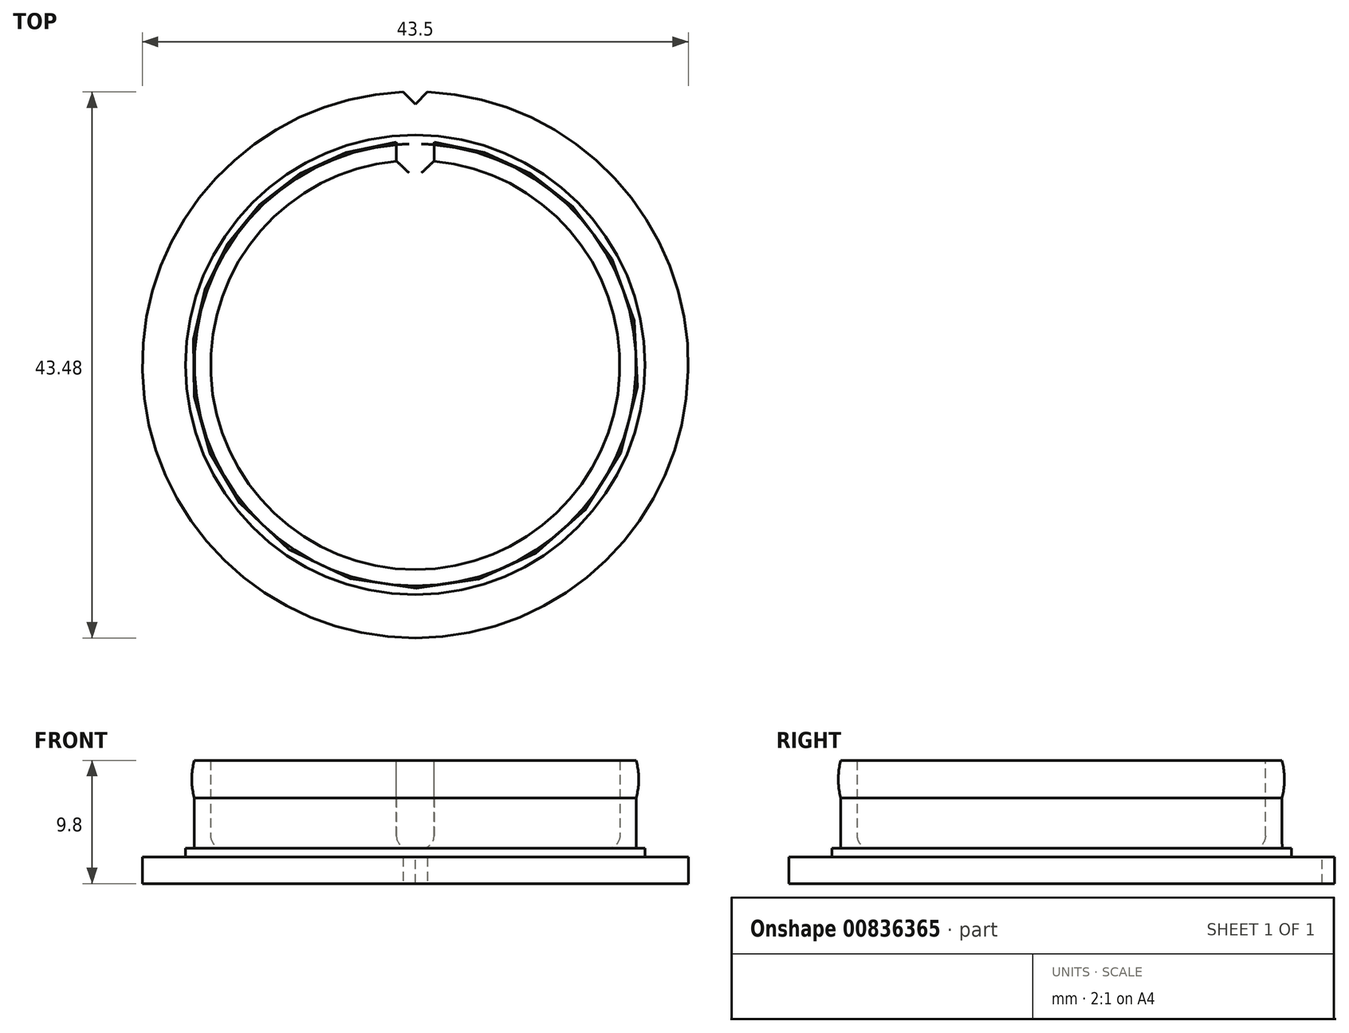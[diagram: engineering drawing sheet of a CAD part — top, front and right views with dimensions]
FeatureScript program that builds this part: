
annotation { "Feature Type Name" : "Feature", "Feature Type Description" : "" }
export const myFeature = defineFeature(function(context is Context, id is Id, definition is map)
    precondition{}
    {
        {
            var Q0;
            Q0=qCreatedBy(makeId("Top.planeOp"),FACE);
            var sketch = newSketch(context, id + "F0", { "sketchPlane" : qUnion([Q0])});
            skCircle(sketch, "E0", {"center": v(0, 0) * mm, "radius": 21.75 * mm});
            skSolve(sketch);
        }
        {
            var Q0;
            Q0 = qSketchRegion(id + "F0", true);
            extrude(context, id + "F1", {"entities" : qUnion([Q0]), "depth" : 2.1 * mm, "offsetDistance" : 25 * mm});
        }
        {
            var Q0;
            Q0=makeQuery(id+"F1.opExtrude","CAP_FACE",FACE,{"disambiguationData":[OSD([sQuery(id+"F0.wireOp",EDGE,"E0")])],"isStart":false});
            var sketch = newSketch(context, id + "F2", { "sketchPlane" : qUnion([Q0])});
            skCircle(sketch, "E1", {"center": v(0, 0) * mm, "radius": 18.3 * mm});
            skSolve(sketch);
        }
        {
            var Q0;
            Q0 = qSketchRegion(id + "F2", true);
            extrude(context, id + "F3", {"entities" : qUnion([Q0]), "operationType" : NewBodyOperationType.ADD, "depth" : .7 * mm, "offsetDistance" : 25 * mm});
        }
        {
            var Q0;
            Q0=makeQuery(id+"F3.opExtrude","CAP_FACE",FACE,{"disambiguationData":[OSD([sQuery(id+"F2.wireOp",EDGE,"E1")])],"isStart":false});
            var sketch = newSketch(context, id + "F4", { "sketchPlane" : qUnion([Q0])});
            skCircle(sketch, "E2", {"center": v(0, 0) * mm, "radius": 17.6 * mm});
            skCircle(sketch, "E3.0", {"center": v(0, 0) * mm, "radius": 16.3 * mm});
            skSolve(sketch);
        }
        {
            var Q0;
            Q0 = qSketchRegion(id + "F4", true);
            extrude(context, id + "F5", {"entities" : qUnion([Q0]), "operationType" : NewBodyOperationType.ADD, "depth" : 7 * mm, "offsetDistance" : 25 * mm});
        }
        {
            var Q0;
            Q0=qCreatedBy(makeId("Front.planeOp"),FACE);
            var sketch = newSketch(context, id + "F6", { "sketchPlane" : qUnion([Q0])});
            skArc(sketch, "E4", {"start": v(-17.6, 9.8) * mm, "mid": v(-17.8, 8.3) * mm, "end": v(-17.6, 6.8) * mm});
            skLineSegment(sketch, "E5", {"start": v(-17.8, 10.53) * mm, "end": v(-17.8, 6.3) * mm, "construction": true});
            skLineSegment(sketch, "E6", {"start": v(-17.6, 9.8) * mm, "end": v(-17.6, 6.8) * mm});
            skSolve(sketch);
        }
        {
            var Q0;
            Q0 = qSketchRegion(id + "F6", true);
            var Q1;
            Q1=makeQuery(id+"F5.opExtrude","SWEPT_FACE",FACE,{"disambiguationData":[OSD([sQuery(id+"F4.wireOp",EDGE,"E2")])]});
            revolve(context, id + "F7", {"operationType" : NewBodyOperationType.ADD, "surfaceOperationType" : NewSurfaceOperationType.NEW, "entities" : qUnion([Q0]), "axis" : qUnion([Q1]), "revolveType" : RevolveType.FULL});
        }
        {
            var Q0;
            Q0=makeQuery(id+"F5.opExtrude","CAP_FACE",FACE,{"disambiguationData":[OSD([sQuery(id+"F4.wireOp",EDGE,"E2"),sQuery(id+"F4.wireOp",EDGE,"E3.0")])],"isStart":false});
            var sketch = newSketch(context, id + "F8", { "sketchPlane" : qUnion([Q0])});
            skLineSegment(sketch, "E7.bottom", {"start": v(-1.5, 19.1) * mm, "end": v(1.5, 19.1) * mm});
            skLineSegment(sketch, "E7.top", {"start": v(-1.5, 16.23) * mm, "end": v(1.5, 16.23) * mm});
            skLineSegment(sketch, "E7.left", {"start": v(-1.5, 19.1) * mm, "end": v(-1.5, 16.23) * mm});
            skLineSegment(sketch, "E7.right", {"start": v(1.5, 19.1) * mm, "end": v(1.5, 16.23) * mm});
            skPoint(sketch, "E8", {"position": v(0, 16.23) * mm});
            skSolve(sketch);
        }
        {
            var Q0;
            Q0 = qSketchRegion(id + "F8", true);
            var Q1;
            {var subQ0=sQuery(id+"F2.wireOp",EDGE,"E1");Q1=makeQuery(id+"F5.boolean.opBoolean","SPLIT",FACE,{"disambiguationData":[TD([makeQuery(id+"F3.opExtrude","SWEPT_FACE",FACE,{"disambiguationData":[OSD([subQ0])]})])],"derivedFrom":makeQuery(id+"F3.opExtrude","CAP_FACE",FACE,{"disambiguationData":[OSD([subQ0])],"isStart":false})});}
            extrude(context, id + "F9", {"entities" : qUnion([Q0]), "operationType" : NewBodyOperationType.REMOVE, "endBound" : BoundingType.UP_TO_SURFACE, "oppositeDirection" : true, "depth" : 25 * mm, "endBoundEntityFace" : qUnion([Q1]), "offsetDistance" : 25 * mm});
        }
        {
            var Q0;
            Q0=makeQuery(id+"F1.opExtrude","CAP_FACE",FACE,{"disambiguationData":[OSD([sQuery(id+"F0.wireOp",EDGE,"E0")])],"isStart":false});
            var sketch = newSketch(context, id + "F10", { "sketchPlane" : qUnion([Q0])});
            skLineSegment(sketch, "E9", {"start": v(0, 20.75) * mm, "end": v(1, 21.75) * mm});
            skLineSegment(sketch, "E10", {"start": v(1, 21.75) * mm, "end": v(-1, 21.75) * mm});
            skLineSegment(sketch, "E11", {"start": v(-1, 21.75) * mm, "end": v(0, 20.75) * mm});
            skSolve(sketch);
        }
        {
            var Q0;
            Q0 = qSketchRegion(id + "F10", true);
            extrude(context, id + "F11", {"entities" : qUnion([Q0]), "operationType" : NewBodyOperationType.REMOVE, "endBound" : BoundingType.THROUGH_ALL, "oppositeDirection" : true, "depth" : 25 * mm, "offsetDistance" : 25 * mm});
        }
        {
            var Q0;
            {var subQ1=sQuery(id+"F8.wireOp",EDGE,"E7.left");var subQ4=makeQuery(id+"F9.boolean.opBoolean","COPY",FACE,{"derivedFrom":makeQuery(id+"F9.opExtrude","SWEPT_FACE",FACE,{"disambiguationData":[OSD([subQ1])]})});var subQ5=sQuery(id+"F4.wireOp",EDGE,"E3.0");Q0=makeQuery(id+"FG1MyRzhxzpAUdr_1.2.F9.boolean.opBoolean","SPLIT",EDGE,{"disambiguationData":[TD([subQ4])],"derivedFrom":makeQuery(id+"FG1MyRzhxzpAUdr_1.1.F9.boolean.opBoolean","SPLIT",EDGE,{"disambiguationData":[TD([subQ4])],"derivedFrom":makeQuery(id+"F5.opExtrude","CAP_EDGE",EDGE,{"disambiguationData":[OSD([subQ5])],"isStart":true})})});}
            var Q1;
            {var subQ0=sQuery(id+"F8.wireOp",EDGE,"E7.right");var subQ2=sQuery(id+"F4.wireOp",EDGE,"E3.0");Q1=makeQuery(id+"FG1MyRzhxzpAUdr_1.1.F9.boolean.opBoolean","SPLIT",EDGE,{"disambiguationData":[TD([makeQuery(id+"F9.boolean.opBoolean","COPY",FACE,{"derivedFrom":makeQuery(id+"F9.opExtrude","SWEPT_FACE",FACE,{"disambiguationData":[OSD([subQ0])]})})])],"derivedFrom":makeQuery(id+"F5.opExtrude","CAP_EDGE",EDGE,{"disambiguationData":[OSD([subQ2])],"isStart":true})});}
            var Q2;
            {var subQ0=sQuery(id+"F8.wireOp",EDGE,"E7.right");var subQ1=sQuery(id+"F8.wireOp",EDGE,"E7.left");var subQ4=makeQuery(id+"FG1MyRzhxzpAUdr_1.1.F9.opExtrude","SWEPT_FACE",FACE,{"disambiguationData":[OSD([subQ0])]});var subQ5=sQuery(id+"F4.wireOp",EDGE,"E3.0");Q2=makeQuery(id+"FG1MyRzhxzpAUdr_1.2.F9.boolean.opBoolean","SPLIT",EDGE,{"disambiguationData":[TD([makeQuery(id+"FG1MyRzhxzpAUdr_1.1.F9.boolean.opBoolean","COPY",FACE,{"derivedFrom":subQ4})])],"derivedFrom":makeQuery(id+"FG1MyRzhxzpAUdr_1.1.F9.boolean.opBoolean","SPLIT",EDGE,{"disambiguationData":[TD([makeQuery(id+"F9.boolean.opBoolean","COPY",FACE,{"derivedFrom":makeQuery(id+"F9.opExtrude","SWEPT_FACE",FACE,{"disambiguationData":[OSD([subQ1])]})})])],"derivedFrom":makeQuery(id+"F5.opExtrude","CAP_EDGE",EDGE,{"disambiguationData":[OSD([subQ5])],"isStart":true})})});}
            var Q3;
            Q3=makeQuery(id+"F9.boolean.opBoolean","COPY",EDGE,{"derivedFrom":makeQuery(id+"F9.opExtrude","CAP_EDGE",EDGE,{"disambiguationData":[OSD([sQuery(id+"F8.wireOp",EDGE,"E7.left")])],"isStart":false})});
            var Q4;
            Q4=makeQuery(id+"F9.boolean.opBoolean","COPY",EDGE,{"derivedFrom":makeQuery(id+"F9.opExtrude","CAP_EDGE",EDGE,{"disambiguationData":[OSD([sQuery(id+"F8.wireOp",EDGE,"E7.right")])],"isStart":false})});
            var Q5;
            Q5=makeQuery(id+"FG1MyRzhxzpAUdr_1.1.F9.boolean.opBoolean","COPY",EDGE,{"derivedFrom":makeQuery(id+"FG1MyRzhxzpAUdr_1.1.F9.opExtrude","CAP_EDGE",EDGE,{"disambiguationData":[OSD([sQuery(id+"F8.wireOp",EDGE,"E7.left")])],"isStart":false})});
            var Q6;
            Q6=makeQuery(id+"FG1MyRzhxzpAUdr_1.2.F9.boolean.opBoolean","COPY",EDGE,{"derivedFrom":makeQuery(id+"FG1MyRzhxzpAUdr_1.2.F9.opExtrude","CAP_EDGE",EDGE,{"disambiguationData":[OSD([sQuery(id+"F8.wireOp",EDGE,"E7.right")])],"isStart":false})});
            var Q7;
            Q7=makeQuery(id+"FG1MyRzhxzpAUdr_1.2.F9.boolean.opBoolean","COPY",EDGE,{"derivedFrom":makeQuery(id+"FG1MyRzhxzpAUdr_1.2.F9.opExtrude","CAP_EDGE",EDGE,{"disambiguationData":[OSD([sQuery(id+"F8.wireOp",EDGE,"E7.left")])],"isStart":false})});
            var Q8;
            Q8=makeQuery(id+"FG1MyRzhxzpAUdr_1.1.F9.boolean.opBoolean","COPY",EDGE,{"derivedFrom":makeQuery(id+"FG1MyRzhxzpAUdr_1.1.F9.opExtrude","CAP_EDGE",EDGE,{"disambiguationData":[OSD([sQuery(id+"F8.wireOp",EDGE,"E7.right")])],"isStart":false})});
            fillet(context, id + "F12", {"entities" : qUnion([Q0, Q1, Q2, Q3, Q4, Q5, Q6, Q7, Q8]), "radius" : 1 * mm, "tangentPropagation" : true, "allowEdgeOverflow" : false});
        }
    });
